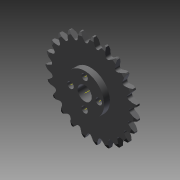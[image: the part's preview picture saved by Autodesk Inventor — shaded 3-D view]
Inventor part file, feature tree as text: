
AUTODESK INVENTOR PART (.ipt)
format: ipt  version: 2015 (Build 190159000, 159)  size: 700,928 bytes
history: native  units: in
note: dims shown in document units (in); Inventor stores cm internally (conversion verified against a paired STEP export)
features: other x14, sketch x1, imported_body x1, projected_geometry x1
ambient origin geometry x8: Origin, YZ Plane, XZ Plane, XY Plane, X Axis, Y Axis, Z Axis, Center Point
bodies: Body1 (feature_tree)
feature tree (17):
  other  "sprocket_25_24t_tetrix_2012"
  other  "sprocket_25_24t_tetrix_20121"
  other  "A_1"
  other  "A_2"
  other  "A_4"
  other  "A_9"
  other  "A_3"
  other  "A_6"
  other  "A_7"
  other  "A_8"
  other  "A_5"
  other  "FRONT"
  other  "TOP"
  other  "RIGHT"
  sketch  "Sketch1"
  imported_body  "Base1"
  projected_geometry  "Projected Loop1"
